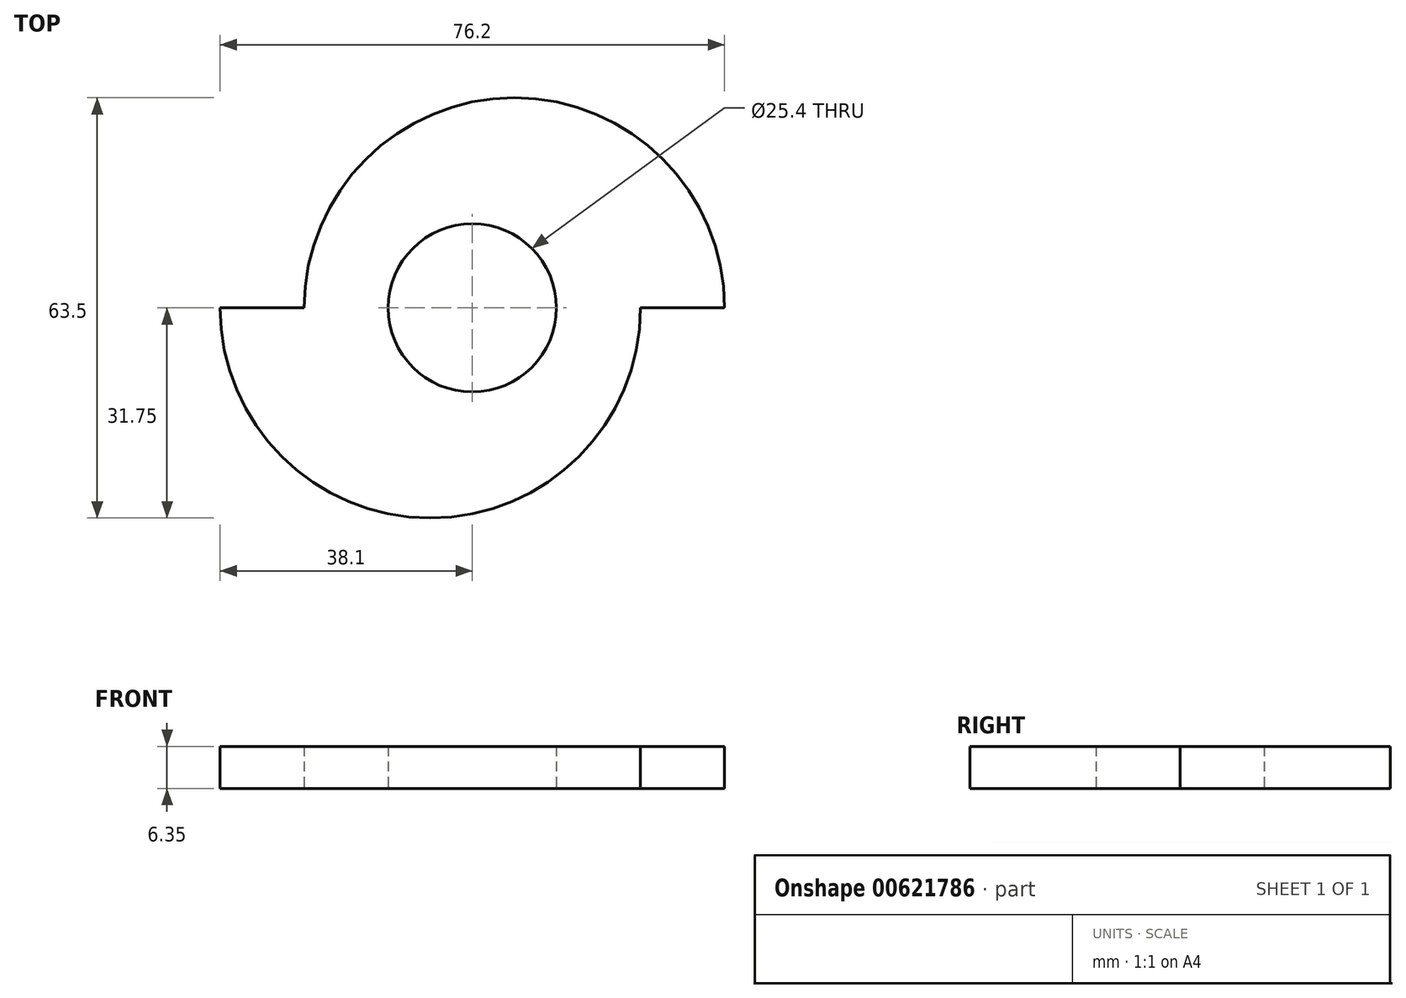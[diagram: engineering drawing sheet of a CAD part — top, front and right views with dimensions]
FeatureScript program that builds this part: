
annotation { "Feature Type Name" : "Feature", "Feature Type Description" : "" }
export const myFeature = defineFeature(function(context is Context, id is Id, definition is map)
    precondition{}
    {
        {
            var Q0;
            Q0=qCreatedBy(makeId("Top.planeOp"),FACE);
            var sketch = newSketch(context, id + "F0", { "sketchPlane" : qUnion([Q0])});
            skCircle(sketch, "E0", {"center": v(0, 0) * mm, "radius": 38.1 * mm});
            skCircle(sketch, "E1", {"center": v(0, 0) * mm, "radius": 12.7 * mm});
            skCircle(sketch, "E2", {"center": v(6.35, 0) * mm, "radius": 31.75 * mm});
            skCircle(sketch, "E3", {"center": v(-6.35, 0) * mm, "radius": 31.75 * mm});
            skLineSegment(sketch, "E4", {"start": v(-38.1, 0) * mm, "end": v(-25.4, 0) * mm});
            skLineSegment(sketch, "E5", {"start": v(-25.4, 0) * mm, "end": v(-25.4, 0) * mm});
            skLineSegment(sketch, "E6", {"start": v(25.4, 0) * mm, "end": v(38.1, 0) * mm});
            skSolve(sketch);
        }
        {
            var Q0;
            {var subQ0=sQuery(id+"F0.wireOp",EDGE,"E4");Q0=makeQuery(id+"F0.imprint","IMPRINT",FACE,{"disambiguationData":[TD([[makeQuery(id+"F0.imprint","IMPRINT",EDGE,{"derivedFrom":subQ0}),-1.0]])]});}
            var Q1;
            Q1=makeQuery(id+"F0.imprint","IMPRINT",FACE,{"disambiguationData":[TD([[makeQuery(id+"F0.imprint","IMPRINT",EDGE,{"derivedFrom":sQuery(id+"F0.wireOp",EDGE,"E1")}),-1.0]])]});
            var Q2;
            {var subQ0=sQuery(id+"F0.wireOp",EDGE,"E6");Q2=makeQuery(id+"F0.imprint","IMPRINT",FACE,{"disambiguationData":[TD([[makeQuery(id+"F0.imprint","IMPRINT",EDGE,{"derivedFrom":subQ0}),1.0]])]});}
            extrude(context, id + "F1", {"entities" : qUnion([Q0, Q1, Q2]), "depth" : 6.35 * mm, "offsetDistance" : 25.4 * mm});
        }
    });
